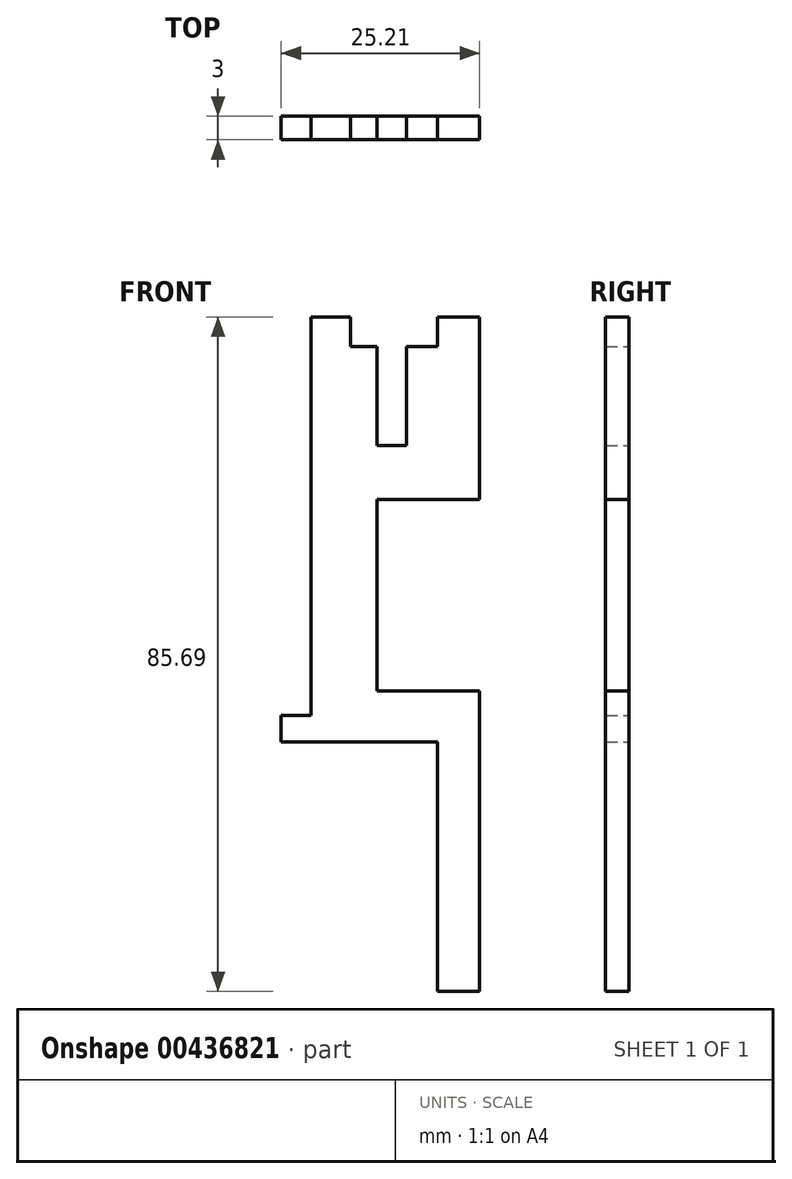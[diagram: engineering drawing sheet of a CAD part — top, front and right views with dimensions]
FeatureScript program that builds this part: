
annotation { "Feature Type Name" : "Feature", "Feature Type Description" : "" }
export const myFeature = defineFeature(function(context is Context, id is Id, definition is map)
    precondition{}
    {
        {
            var Q0;
            Q0=qCreatedBy(makeId("Front.planeOp"),FACE);
            var sketch = newSketch(context, id + "F0", { "sketchPlane" : qUnion([Q0])});
            skLineSegment(sketch, "E0", {"start": v(0, 0) * mm, "end": v(5.33, 0) * mm});
            skLineSegment(sketch, "E1", {"start": v(5.33, 0) * mm, "end": v(5.33, 38.2) * mm});
            skLineSegment(sketch, "E2", {"start": v(5.33, 38.2) * mm, "end": v(-7.7, 38.2) * mm});
            skLineSegment(sketch, "E3", {"start": v(-7.7, 38.2) * mm, "end": v(-7.7, 62.47) * mm});
            skLineSegment(sketch, "E4", {"start": v(-7.7, 62.47) * mm, "end": v(5.33, 62.47) * mm});
            skLineSegment(sketch, "E5", {"start": v(5.33, 62.47) * mm, "end": v(5.33, 85.69) * mm});
            skLineSegment(sketch, "E6", {"start": v(5.33, 85.69) * mm, "end": v(0, 85.69) * mm});
            skLineSegment(sketch, "E7", {"start": v(0, 85.69) * mm, "end": v(0, 81.92) * mm});
            skLineSegment(sketch, "E8", {"start": v(0, 81.92) * mm, "end": v(-3.97, 81.92) * mm});
            skLineSegment(sketch, "E9", {"start": v(-3.97, 81.92) * mm, "end": v(-3.97, 69.36) * mm});
            skLineSegment(sketch, "E10", {"start": v(-3.97, 69.36) * mm, "end": v(-7.7, 69.36) * mm});
            skLineSegment(sketch, "E11", {"start": v(-7.7, 69.36) * mm, "end": v(-7.7, 81.92) * mm});
            skLineSegment(sketch, "E12", {"start": v(-7.7, 81.92) * mm, "end": v(-11.08, 81.92) * mm});
            skLineSegment(sketch, "E13", {"start": v(-11.08, 81.92) * mm, "end": v(-11.08, 85.69) * mm});
            skLineSegment(sketch, "E14", {"start": v(-11.08, 85.69) * mm, "end": v(-16.1, 85.69) * mm});
            skLineSegment(sketch, "E15", {"start": v(-16.1, 85.69) * mm, "end": v(-16.1, 35.03) * mm});
            skLineSegment(sketch, "E16", {"start": v(-16.1, 35.03) * mm, "end": v(-19.88, 35.03) * mm});
            skLineSegment(sketch, "E17", {"start": v(-19.88, 35.03) * mm, "end": v(-19.88, 31.68) * mm});
            skLineSegment(sketch, "E18", {"start": v(-19.88, 31.68) * mm, "end": v(0, 31.68) * mm});
            skLineSegment(sketch, "E19", {"start": v(0, 31.68) * mm, "end": v(0, 0) * mm});
            skSolve(sketch);
        }
        {
            var Q0;
            Q0=makeQuery(id+"F0.imprint","IMPRINT",FACE,{"disambiguationData":[TD([[makeQuery(id+"F0.imprint","IMPRINT",EDGE,{"derivedFrom":sQuery(id+"F0.wireOp",EDGE,"E0")}),1.0]])]});
            extrude(context, id + "F1", {"entities" : qUnion([Q0]), "depth" : 3 * mm});
        }
    });
